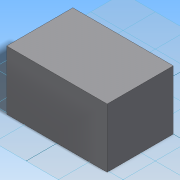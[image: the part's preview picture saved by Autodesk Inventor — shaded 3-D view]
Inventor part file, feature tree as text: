
AUTODESK INVENTOR PART (.ipt)
format: ipt  version: 2014 SP2 (Build 180246200, 246)  size: 76,800 bytes
history: native  units: in
note: dims shown in document units (in); Inventor stores cm internally (conversion verified against a paired STEP export)
features: extrude x1, sketch x1
ambient origin geometry x8: Origin, YZ Plane, XZ Plane, XY Plane, X Axis, Y Axis, Z Axis, Center Point
bodies: Solid1 (feature_tree)
feature tree (2):
  extrude  "Extrusion1"  Depth=1.8307in
  sketch  "Sketch1"  dims[d0=3.1102in d1=1.8307in d2=2.0472in d3=0.0in]
